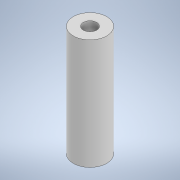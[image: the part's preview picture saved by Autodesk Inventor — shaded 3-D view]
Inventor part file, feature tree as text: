
AUTODESK INVENTOR PART (.ipt)
format: ipt  version: 2022 (Build 260153000, 153)  size: 99,328 bytes
history: native  units: mm
features: revolve x1, sketch x1
ambient origin geometry x8: Origin, YZ Plane, XZ Plane, XY Plane, X Axis, Y Axis, Z Axis, Center Point
bodies: Solid1 (feature_tree)
feature tree (2):
  revolve  "Revolution1"  [1 undecoded]
  sketch  "Sketch1"  dims[d0=16.5mm d1=1.0mm d2=1.5mm d3=90.0deg]
note: 1 required parameter value undecoded (feature->parameter linkage not recoverable at this tier; creation-order binding heuristic only, values carry confidence <= 0.55)
